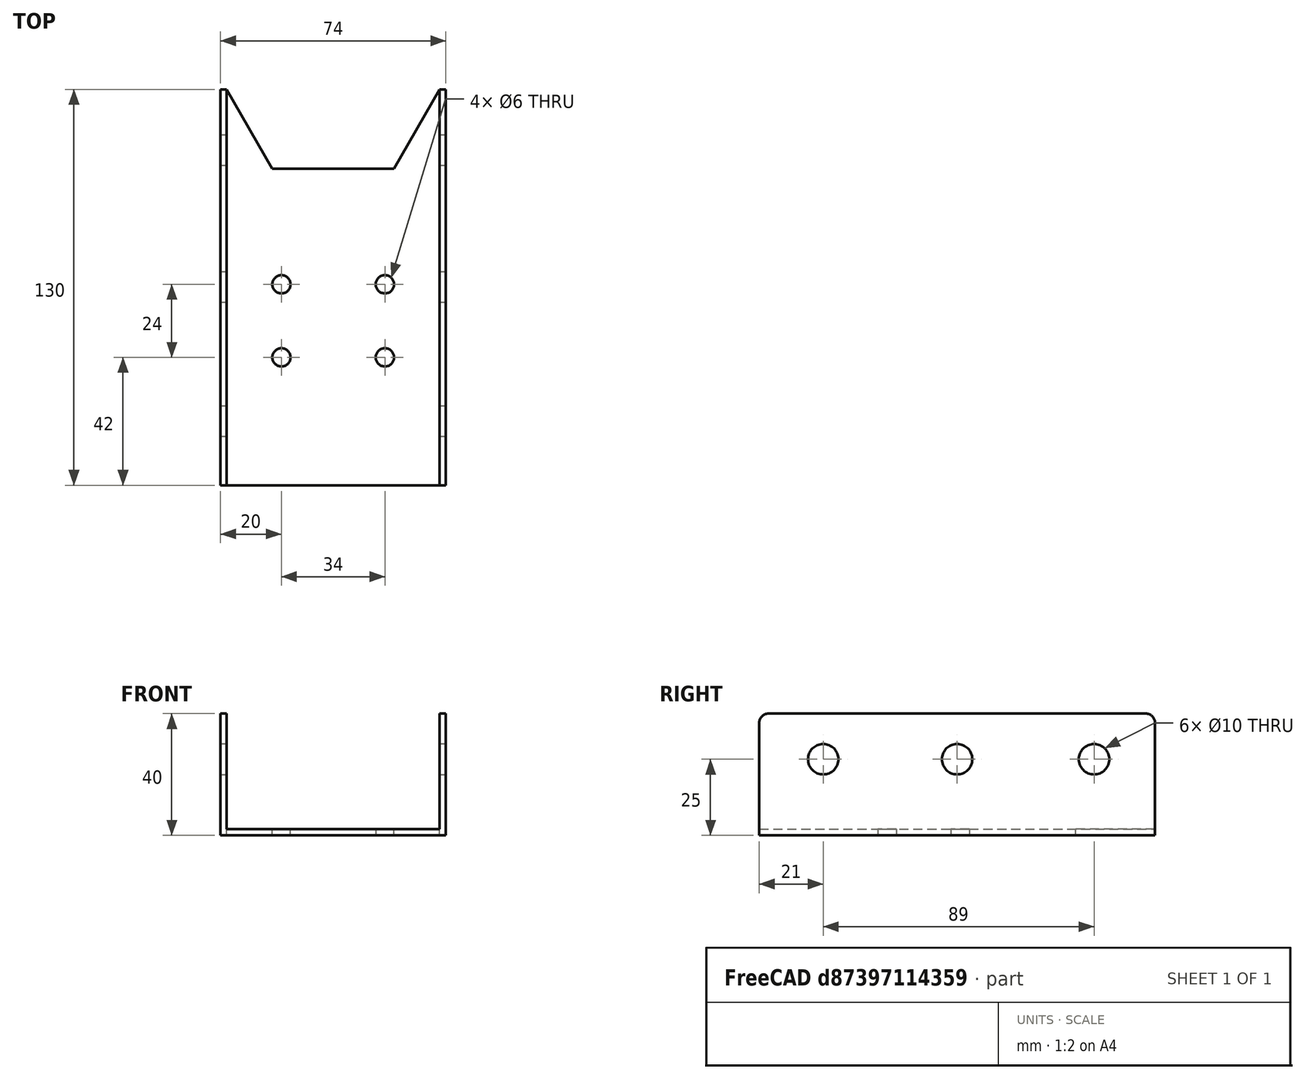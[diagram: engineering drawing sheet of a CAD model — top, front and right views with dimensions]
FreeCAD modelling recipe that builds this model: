
FCSTD DOCUMENT  (FreeCAD 1.0R38641 +678 (Git))
Label: drzak radio
License: All rights reserved
LicenseURL: https://en.wikipedia.org/wiki/All_rights_reserved
objects: TechDraw::DrawViewDimension×16, TechDraw::DrawProjGroupItem×4, Part::MultiFuse×3, Part::Cylinder×3, Part::Box×2, Sketcher::SketchObject×1, Part::Extrusion×1, Part::Cut×1, TechDraw::DrawSVGTemplate×1, Part::Fillet×1, TechDraw::DrawProjGroup×1, TechDraw::DrawPage×1
note: 38 computed .brp shape members not serialized (recipe doc carries the construction recipe); baked Part::Feature solids carry a one-line shape summary decoded from their .brp

FEATURE [Sketcher::SketchObject] Sketch
  ArcFitTolerance = 1e-06
  FullyConstrained = true
  MakeInternals = false
  sketch-geometry (15):
    g0: LineSegment StartX=0 StartY=130 StartZ=0 EndX=0 EndY=0 EndZ=0
    g1: LineSegment StartX=0 StartY=0 StartZ=0 EndX=70 EndY=0 EndZ=0
    g2: LineSegment StartX=70 StartY=0 StartZ=0 EndX=70 EndY=130 EndZ=0
    g3: LineSegment StartX=70 StartY=130 StartZ=0 EndX=55 EndY=104 EndZ=0
    g4: LineSegment StartX=55 StartY=104 StartZ=0 EndX=15 EndY=104 EndZ=0
    g5: LineSegment StartX=15 StartY=104 StartZ=0 EndX=0 EndY=130 EndZ=0
    g6: LineSegment [constr] StartX=0 StartY=130 StartZ=0 EndX=70 EndY=130 EndZ=0
    g7: Circle CenterX=52 CenterY=66 CenterZ=0 NormalX=0 NormalY=0 NormalZ=1 AngleXU=0 Radius=3
    g8: Circle CenterX=18 CenterY=42 CenterZ=0 NormalX=0 NormalY=0 NormalZ=1 AngleXU=0 Radius=3
    g9: Circle CenterX=52 CenterY=42 CenterZ=0 NormalX=0 NormalY=0 NormalZ=1 AngleXU=0 Radius=3
    g10: Circle CenterX=18 CenterY=66 CenterZ=0 NormalX=0 NormalY=0 NormalZ=1 AngleXU=0 Radius=3
    g11: LineSegment [constr] StartX=18 StartY=66 StartZ=0 EndX=18 EndY=42 EndZ=0
    g12: LineSegment [constr] StartX=18 StartY=42 StartZ=0 EndX=52 EndY=42 EndZ=0
    g13: LineSegment [constr] StartX=52 StartY=42 StartZ=0 EndX=52 EndY=66 EndZ=0
    g14: LineSegment [constr] StartX=52 StartY=66 StartZ=0 EndX=18 EndY=66 EndZ=0
  constraints (39):
    c: Vertical(g0)
    c: Coincident(g0,g1)
    c: Horizontal(g1)
    c: Coincident(g1,g2)
    c: Vertical(g2)
    c: Coincident(g3,g4)
    c: Horizontal(g4)
    c: Coincident(g4,g5)
    c: Coincident(g6,g5)
    c: Horizontal(g6)
    c: DistanceY(g0,g0) = 130
    c: DistanceX(g1,g1) = 70
    c: DistanceX(g4,g4) = 40
    c: Coincident(g2,g3)
    c: Coincident(g2,g6)
    c: Coincident(g0,g5)
    c: DistanceY(g3,g3) = 26
    c: Coincident(g0,g-1)
    c: Distance(g4,g0) = 15
    c: Diameter(g10) = 6
    c: Coincident(g11,g12)
    c: Coincident(g12,g13)
    c: Coincident(g13,g14)
    c: Coincident(g14,g11)
    c: Vertical(g11)
    c: Vertical(g13)
    c: Horizontal(g12)
    c: Horizontal(g14)
    c: Coincident(g11,g10)
    c: Coincident(g12,g9)
    c: Coincident(g11,g8)
    c: Coincident(g7,g13)
    c: Equal(g10,g7)
    c: Equal(g7,g9)
    c: Equal(g9,g8)
    c: DistanceY(g9,g7) = 24
    c: DistanceX(g8,g9) = 34
    c: Distance(g10,g4) = 38
    c: Distance(g8,g0) = 18
FEATURE [Part::Extrusion] Extrude
  Base = -> Sketch
  Dir = (0,0,1)
  DirMode = 2
  FaceMakerClass = Part::FaceMakerBullseye
  FaceMakerMode = 3
  LengthFwd = 2
  LengthRev = 0
  Solid = true
  Symmetric = false
FEATURE [Part::Box] Box  label="Krychle"
  AttacherType = Attacher::AttachEngine3D
  Height = 40
  Length = 2
  Placement = pos=(-2,0,0) rot=(0,0,1;0rad)
  Width = 130
FEATURE [Part::Box] Box001  label="Krychle001"
  AttacherType = Attacher::AttachEngine3D
  Height = 40
  Length = 2
  Placement = pos=(70,0,0) rot=(0,0,1;0rad)
  Width = 130
FEATURE [Part::MultiFuse] Fusion
  Refine = true
  Shapes = -> [Box,Box001]
FEATURE [Part::Cylinder] Cylinder  label="Válec"
  Angle = 360
  AttacherType = Attacher::AttachEngine3D
  FirstAngle = 0
  Height = 100
  Placement = pos=(-10,110,25) rot=(0,1,0;1.5708rad)
  Radius = 5
  SecondAngle = 0
FEATURE [Part::Cylinder] Cylinder001  label="Válec001"
  Angle = 360
  AttacherType = Attacher::AttachEngine3D
  FirstAngle = 0
  Height = 100
  Placement = pos=(-10,65,25) rot=(0,1,0;1.5708rad)
  Radius = 5
  SecondAngle = 0
FEATURE [Part::Cylinder] Cylinder002  label="Válec002"
  Angle = 360
  AttacherType = Attacher::AttachEngine3D
  FirstAngle = 0
  Height = 100
  Placement = pos=(-10,21,25) rot=(0,1,0;1.5708rad)
  Radius = 5
  SecondAngle = 0
FEATURE [Part::MultiFuse] Fusion001
  Refine = true
  Shapes = -> [Cylinder,Cylinder001,Cylinder002]
FEATURE [Part::Cut] Cut
  Base = -> Fusion
  Refine = true
  Tool = -> Fusion001
FEATURE [Part::MultiFuse] Fusion002
  Refine = true
  Shapes = -> [Extrude,Cut]
FEATURE [TechDraw::DrawSVGTemplate] Template  label="Šablona"
  Height = 210
  Orientation = 1
  Template = /snap/freecad/1634/usr/share/Mod/TechDraw/Templates/Default_Template_A4_Landscape.svg
  Width = 297
FEATURE [Part::Fillet] Fillet
  Base = -> Fusion002
  EdgeLinks = -> Fusion002 [Edge9,Edge10,Edge33,Edge34]
  Edges = 4 edges r=3: [Edge9,Edge10,Edge33,Edge34]
FEATURE [TechDraw::DrawProjGroupItem] View  label="Front"
  CoarseView = false
  Direction = (0,-1,0)
  Focus = 100
  HardHidden = false
  IsoCount = 0
  IsoHidden = false
  IsoVisible = false
  LockPosition = true
  Perspective = false
  Rotation = 0
  RotationVector = (1,0,0)
  ScaleType = 2
  ScrubCount = 1
  SeamHidden = false
  SeamVisible = false
  SmoothHidden = false
  SmoothVisible = true
  Source = -> [Fillet]
  Type = 0
  X = 0
  XDirection = (1,0,0)
  Y = 0
FEATURE [TechDraw::DrawProjGroupItem] ProjItem001  label="Dole"
  CoarseView = false
  Direction = (0,0,-1)
  Focus = 100
  HardHidden = false
  IsoCount = 0
  IsoHidden = false
  IsoVisible = false
  LockPosition = false
  Perspective = false
  Rotation = 0
  RotationVector = (1,0,0)
  ScaleType = 0
  ScrubCount = 1
  SeamHidden = false
  SeamVisible = false
  SmoothHidden = false
  SmoothVisible = true
  Source = -> [Fillet]
  Type = 5
  X = 0
  XDirection = (1,0,0)
  Y = 100
FEATURE [TechDraw::DrawProjGroupItem] ProjItem002  label="Vlevo"
  CoarseView = false
  Direction = (-1,-1e-16,0)
  Focus = 100
  HardHidden = false
  IsoCount = 0
  IsoHidden = false
  IsoVisible = false
  LockPosition = false
  Perspective = false
  Rotation = 0
  RotationVector = (1,0,0)
  ScaleType = 0
  ScrubCount = 1
  SeamHidden = false
  SeamVisible = false
  SmoothHidden = false
  SmoothVisible = true
  Source = -> [Fillet]
  Type = 1
  X = 124.125
  XDirection = (1e-16,-1,0)
  Y = 0
FEATURE [TechDraw::DrawProjGroupItem] ProjItem  label="FrontTopLeft"
  CoarseView = false
  Direction = (-0.57735,-0.57735,0.57735)
  Focus = 100
  HardHidden = false
  IsoCount = 0
  IsoHidden = false
  IsoVisible = false
  LockPosition = false
  Perspective = false
  Rotation = 0
  RotationVector = (1,0,0)
  ScaleType = 0
  ScrubCount = 1
  SeamHidden = false
  SeamVisible = false
  SmoothHidden = false
  SmoothVisible = true
  Source = -> [Fillet]
  Type = 6
  X = 124.125
  XDirection = (0.707107,-0.707107,0)
  Y = -92.5034
FEATURE [TechDraw::DrawProjGroup] ProjGroup
  Anchor = -> View
  AutoDistribute = true
  LockPosition = false
  ProjectionType = 0
  Rotation = 0
  ScaleType = 0
  Source = -> [Fillet]
  Views = -> [View,ProjItem001,ProjItem002,ProjItem]
  X = 63.8714
  Y = 38.1827
  spacingX = 15
  spacingY = 15
FEATURE [TechDraw::DrawViewDimension] Dimension010  label="Rozměr010"
  AngleOverride = false
  Arbitrary = false
  ArbitraryTolerances = false
  BoxCorners = (2) [(-65,-20,0),(65,20,0)]
  EqualTolerance = true
  ExtensionAngle = 0
  FormatSpec = %.2w
  FormatSpecOverTolerance = %+.2w
  FormatSpecUnderTolerance = %+.2w
  Inverted = false
  LineAngle = 0
  LockPosition = false
  MeasureType = 1
  OverTolerance = 0
  References2D = -> [ProjItem002]
  Rotation = 0
  ScaleType = 0
  TheoreticalExact = false
  Type = 0
  UnderTolerance = 0
  X = -22.5
  Y = 1.6956
FEATURE [TechDraw::DrawViewDimension] Dimension011  label="Rozměr011"
  AngleOverride = false
  Arbitrary = false
  ArbitraryTolerances = false
  BoxCorners = (2) [(-65,-20,0),(65,20,0)]
  EqualTolerance = true
  ExtensionAngle = 0
  FormatSpec = %.2w
  FormatSpecOverTolerance = %+.2w
  FormatSpecUnderTolerance = %+.2w
  Inverted = false
  LineAngle = 0
  LockPosition = false
  MeasureType = 1
  OverTolerance = 0
  References2D = -> [ProjItem002]
  Rotation = 0
  ScaleType = 0
  TheoreticalExact = false
  Type = 0
  UnderTolerance = 0
  X = 22
  Y = 1.6956
FEATURE [TechDraw::DrawViewDimension] Dimension014  label="Rozměr014"
  AngleOverride = false
  Arbitrary = false
  ArbitraryTolerances = false
  BoxCorners = (2) [(-37,-65,0),(37,65,0)]
  EqualTolerance = true
  ExtensionAngle = 0
  FormatSpec = ⌀%.2w
  FormatSpecOverTolerance = %+.2w
  FormatSpecUnderTolerance = %+.2w
  Inverted = false
  LineAngle = 0
  LockPosition = false
  MeasureType = 1
  OverTolerance = 0
  References2D = -> [ProjItem001]
  Rotation = 0
  ScaleType = 0
  TheoreticalExact = false
  Type = 5
  UnderTolerance = 0
  X = -10.8949
  Y = 36.3511
FEATURE [TechDraw::DrawViewDimension] Dimension016  label="Rozměr016"
  AngleOverride = false
  Arbitrary = false
  ArbitraryTolerances = false
  BoxCorners = (2) [(-37,-65,0),(37,65,0)]
  EqualTolerance = true
  ExtensionAngle = 0
  FormatSpec = %.2w
  FormatSpecOverTolerance = %+.2w
  FormatSpecUnderTolerance = %+.2w
  Inverted = false
  LineAngle = 0
  LockPosition = false
  MeasureType = 1
  OverTolerance = 0
  References2D = -> [ProjItem001]
  Rotation = 0
  ScaleType = 0
  TheoreticalExact = false
  Type = 0
  UnderTolerance = 0
  X = 42.4402
  Y = 11
FEATURE [TechDraw::DrawViewDimension] Dimension017  label="Rozměr017"
  AngleOverride = false
  Arbitrary = false
  ArbitraryTolerances = false
  BoxCorners = (2) [(-37,-65,0),(37,65,0)]
  EqualTolerance = true
  ExtensionAngle = 0
  FormatSpec = %.2w
  FormatSpecOverTolerance = %+.2w
  FormatSpecUnderTolerance = %+.2w
  Inverted = false
  LineAngle = 0
  LockPosition = false
  MeasureType = 1
  OverTolerance = 0
  References2D = -> [ProjItem001]
  Rotation = 0
  ScaleType = 0
  TheoreticalExact = false
  Type = 0
  UnderTolerance = 0
  X = 42.4402
  Y = 44
FEATURE [TechDraw::DrawViewDimension] Dimension018  label="Rozměr018"
  AngleOverride = false
  Arbitrary = false
  ArbitraryTolerances = false
  BoxCorners = (2) [(-65,-20,0),(65,20,0)]
  EqualTolerance = true
  ExtensionAngle = 0
  FormatSpec = ⌀%.2w
  FormatSpecOverTolerance = %+.2w
  FormatSpecUnderTolerance = %+.2w
  Inverted = false
  LineAngle = 0
  LockPosition = false
  MeasureType = 1
  OverTolerance = 0
  References2D = -> [ProjItem002]
  Rotation = 0
  ScaleType = 0
  TheoreticalExact = false
  Type = 5
  UnderTolerance = 0
  X = 60.6444
  Y = -3.52529
FEATURE [TechDraw::DrawViewDimension] Dimension  label="Rozměr"
  AngleOverride = false
  Arbitrary = false
  ArbitraryTolerances = false
  BoxCorners = (2) [(-37,-20,-1e-07),(37,20,1e-07)]
  EqualTolerance = true
  ExtensionAngle = 0
  FormatSpec = %.2w
  FormatSpecOverTolerance = %+.2w
  FormatSpecUnderTolerance = %+.2w
  Inverted = false
  LineAngle = 0
  LockPosition = false
  MeasureType = 1
  OverTolerance = 0
  References2D = -> [View]
  Rotation = 0
  ScaleType = 0
  TheoreticalExact = false
  Type = 1
  UnderTolerance = 0
  X = 0
  Y = 4.7377
FEATURE [TechDraw::DrawViewDimension] Dimension020  label="Rozměr020"
  AngleOverride = false
  Arbitrary = false
  ArbitraryTolerances = false
  BoxCorners = (2) [(-37,-20,-1e-07),(37,20,1e-07)]
  EqualTolerance = true
  ExtensionAngle = 0
  FormatSpec = %.2w
  FormatSpecOverTolerance = %+.2w
  FormatSpecUnderTolerance = %+.2w
  Inverted = false
  LineAngle = 0
  LockPosition = false
  MeasureType = 1
  OverTolerance = 0
  References2D = -> [View]
  Rotation = 0
  ScaleType = 0
  TheoreticalExact = false
  Type = 0
  UnderTolerance = 0
  X = 42.3076
  Y = 4.7377
FEATURE [TechDraw::DrawViewDimension] Dimension021  label="Rozměr021"
  AngleOverride = false
  Arbitrary = false
  ArbitraryTolerances = false
  BoxCorners = (2) [(-37,-65,0),(37,65,0)]
  EqualTolerance = true
  ExtensionAngle = 0
  FormatSpec = %.2w
  FormatSpecOverTolerance = %+.2w
  FormatSpecUnderTolerance = %+.2w
  Inverted = false
  LineAngle = 0
  LockPosition = false
  MeasureType = 1
  OverTolerance = 0
  References2D = -> [ProjItem001]
  Rotation = 0
  ScaleType = 0
  TheoreticalExact = false
  Type = 0
  UnderTolerance = 0
  X = -7.70088
  Y = -8.86946
FEATURE [TechDraw::DrawViewDimension] Dimension022  label="Rozměr022"
  AngleOverride = false
  Arbitrary = false
  ArbitraryTolerances = false
  BoxCorners = (2) [(-37,-65,0),(37,65,0)]
  EqualTolerance = true
  ExtensionAngle = 0
  FormatSpec = %.2w
  FormatSpecOverTolerance = %+.2w
  FormatSpecUnderTolerance = %+.2w
  Inverted = false
  LineAngle = 0
  LockPosition = false
  MeasureType = 1
  OverTolerance = 0
  References2D = -> [ProjItem001]
  Rotation = 0
  ScaleType = 0
  TheoreticalExact = false
  Type = 1
  UnderTolerance = 0
  X = -7.80547
  Y = -25.8701
FEATURE [TechDraw::DrawViewDimension] Dimension023  label="Rozměr023"
  AngleOverride = false
  Arbitrary = false
  ArbitraryTolerances = false
  BoxCorners = (2) [(-37,-65,0),(37,65,0)]
  EqualTolerance = true
  ExtensionAngle = 0
  FormatSpec = %.2w
  FormatSpecOverTolerance = %+.2w
  FormatSpecUnderTolerance = %+.2w
  Inverted = false
  LineAngle = 0
  LockPosition = false
  MeasureType = 1
  OverTolerance = 0
  References2D = -> [ProjItem001]
  Rotation = 0
  ScaleType = 0
  TheoreticalExact = false
  Type = 2
  UnderTolerance = 0
  X = 7.2447
  Y = -52
FEATURE [TechDraw::DrawViewDimension] Dimension024  label="Rozměr024"
  AngleOverride = false
  Arbitrary = false
  ArbitraryTolerances = false
  BoxCorners = (2) [(-37,-65,0),(37,65,0)]
  EqualTolerance = true
  ExtensionAngle = 0
  FormatSpec = %.2w
  FormatSpecOverTolerance = %+.2w
  FormatSpecUnderTolerance = %+.2w
  Inverted = false
  LineAngle = 0
  LockPosition = false
  MeasureType = 1
  OverTolerance = 0
  References2D = -> [ProjItem001]
  Rotation = 0
  ScaleType = 0
  TheoreticalExact = false
  Type = 2
  UnderTolerance = 0
  X = -52.2637
  Y = 6.95021
FEATURE [TechDraw::DrawViewDimension] Dimension025  label="Rozměr025"
  AngleOverride = false
  Arbitrary = false
  ArbitraryTolerances = false
  BoxCorners = (2) [(-65,-20,0),(65,20,0)]
  EqualTolerance = true
  ExtensionAngle = 0
  FormatSpec = %.2w
  FormatSpecOverTolerance = %+.2w
  FormatSpecUnderTolerance = %+.2w
  Inverted = false
  LineAngle = 0
  LockPosition = false
  MeasureType = 1
  OverTolerance = 0
  References2D = -> [ProjItem002]
  Rotation = 0
  ScaleType = 0
  TheoreticalExact = false
  Type = 0
  UnderTolerance = 0
  X = -55
  Y = 1.6956
FEATURE [TechDraw::DrawViewDimension] Dimension026  label="Rozměr026"
  AngleOverride = false
  Arbitrary = false
  ArbitraryTolerances = false
  BoxCorners = (2) [(-65,-20,0),(65,20,0)]
  EqualTolerance = true
  ExtensionAngle = 0
  FormatSpec = %.2w
  FormatSpecOverTolerance = %+.2w
  FormatSpecUnderTolerance = %+.2w
  Inverted = false
  LineAngle = 0
  LockPosition = false
  MeasureType = 1
  OverTolerance = 0
  References2D = -> [ProjItem002]
  Rotation = 0
  ScaleType = 0
  TheoreticalExact = false
  Type = 0
  UnderTolerance = 0
  X = -39.5182
  Y = 12.5
FEATURE [TechDraw::DrawViewDimension] Dimension027  label="Rozměr027"
  AngleOverride = false
  Arbitrary = false
  ArbitraryTolerances = false
  BoxCorners = (2) [(-65,-20,0),(65,20,0)]
  EqualTolerance = true
  ExtensionAngle = 0
  FormatSpec = %.2w
  FormatSpecOverTolerance = %+.2w
  FormatSpecUnderTolerance = %+.2w
  Inverted = false
  LineAngle = 0
  LockPosition = false
  MeasureType = 1
  OverTolerance = 0
  References2D = -> [ProjItem002]
  Rotation = 0
  ScaleType = 0
  TheoreticalExact = false
  Type = 0
  UnderTolerance = 0
  X = 74.1357
  Y = 0
FEATURE [TechDraw::DrawViewDimension] Dimension028  label="Rozměr028"
  AngleOverride = false
  Arbitrary = false
  ArbitraryTolerances = false
  BoxCorners = (2) [(-65,-20,0),(65,20,0)]
  EqualTolerance = true
  ExtensionAngle = 0
  FormatSpec = R%.2w
  FormatSpecOverTolerance = %+.2w
  FormatSpecUnderTolerance = %+.2w
  Inverted = false
  LineAngle = 0
  LockPosition = false
  MeasureType = 1
  OverTolerance = 0
  References2D = -> [ProjItem002]
  Rotation = 0
  ScaleType = 0
  TheoreticalExact = false
  Type = 4
  UnderTolerance = 0
  X = -70.5201
  Y = 27.3123
FEATURE [TechDraw::DrawPage] Page  label="Stránka"
  KeepUpdated = true
  NextBalloonIndex = 1
  ProjectionType = 0
  Template = -> Template
  Views = -> [ProjGroup,Dimension010,Dimension011,Dimension014,Dimension016,Dimension017,Dimension018,Dimension,Dimension020,Dimension021,Dimension022,Dimension023,Dimension024,Dimension025,Dimension026,Dimension027,Dimension028]
